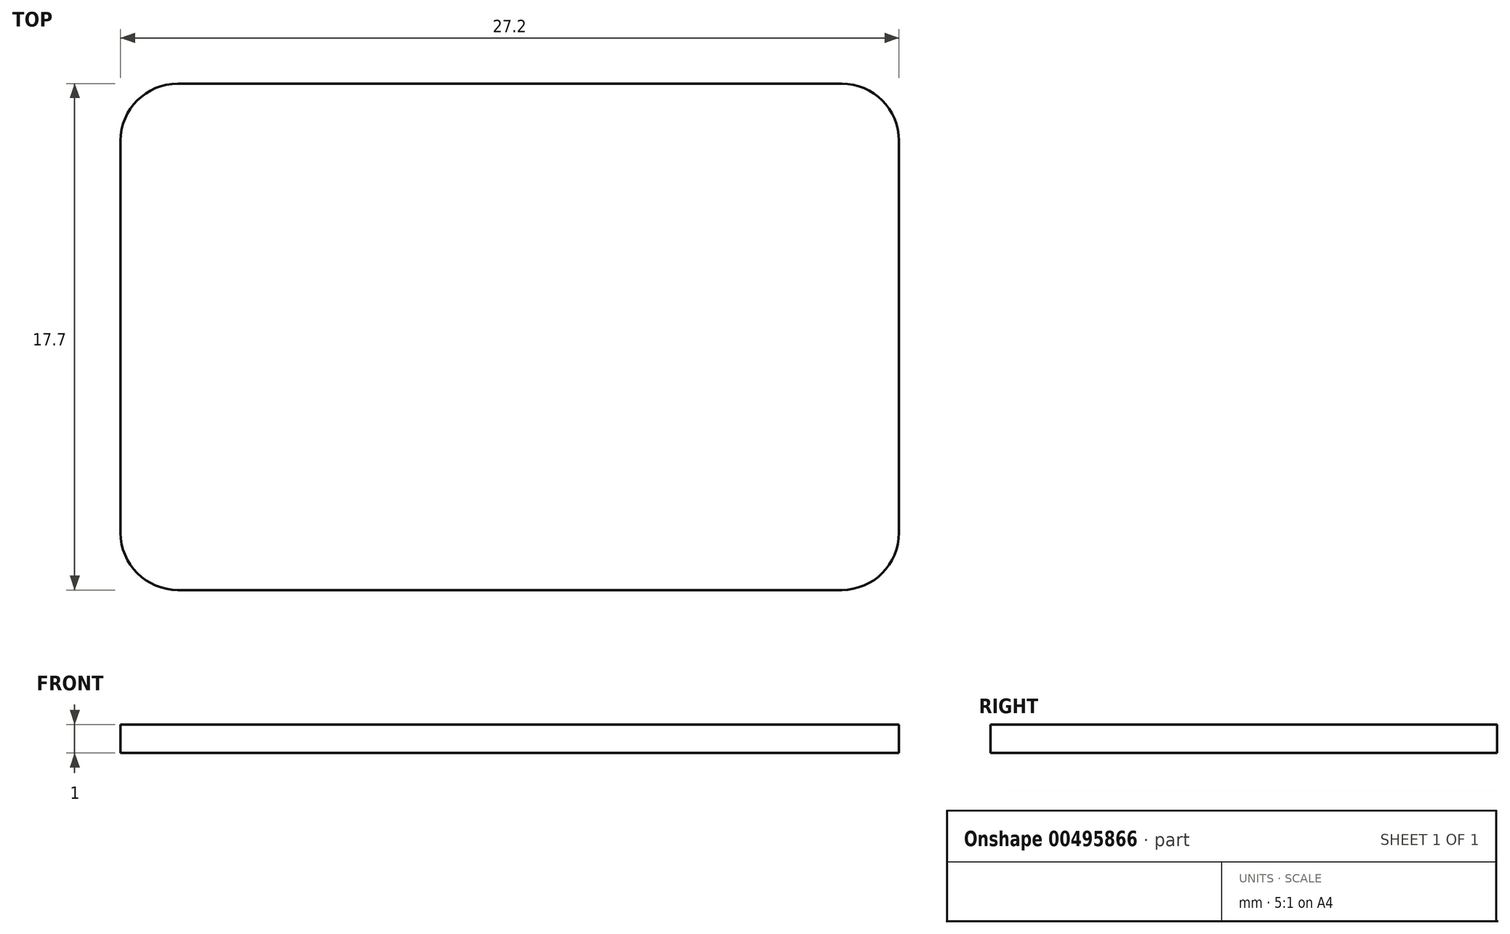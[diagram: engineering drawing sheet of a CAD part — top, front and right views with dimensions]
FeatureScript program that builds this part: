
annotation { "Feature Type Name" : "Feature", "Feature Type Description" : "" }
export const myFeature = defineFeature(function(context is Context, id is Id, definition is map)
    precondition{}
    {
        {
            var Q0;
            Q0=qCreatedBy(makeId("Top.planeOp"),FACE);
            var sketch = newSketch(context, id + "F0", { "sketchPlane" : qUnion([Q0])});
            skLineSegment(sketch, "E0.bottom", {"start": v(11.6, 8.85) * mm, "end": v(-11.6, 8.85) * mm});
            skLineSegment(sketch, "E0.top", {"start": v(11.6, -8.85) * mm, "end": v(-11.6, -8.85) * mm});
            skLineSegment(sketch, "E0.left", {"start": v(13.6, 6.85) * mm, "end": v(13.6, -6.85) * mm});
            skLineSegment(sketch, "E0.right", {"start": v(-13.6, 6.85) * mm, "end": v(-13.6, -6.85) * mm});
            skPoint(sketch, "E0.middle", {"position": v(0, 0) * mm});
            skPoint(sketch, "E1.visualSharp", {"position": v(13.6, 8.85) * mm});
            skArc(sketch, "E1.filletArc", {"start": v(13.6, 6.85) * mm, "mid": v(13.01, 8.26) * mm, "end": v(11.6, 8.85) * mm});
            skPoint(sketch, "E2.visualSharp", {"position": v(13.6, -8.85) * mm});
            skArc(sketch, "E2.filletArc", {"start": v(11.6, -8.85) * mm, "mid": v(13.01, -8.26) * mm, "end": v(13.6, -6.85) * mm});
            skPoint(sketch, "E3.visualSharp", {"position": v(-13.6, -8.85) * mm});
            skArc(sketch, "E3.filletArc", {"start": v(-13.6, -6.85) * mm, "mid": v(-13.01, -8.26) * mm, "end": v(-11.6, -8.85) * mm});
            skPoint(sketch, "E4.visualSharp", {"position": v(-13.6, 8.85) * mm});
            skArc(sketch, "E4.filletArc", {"start": v(-11.6, 8.85) * mm, "mid": v(-13.01, 8.26) * mm, "end": v(-13.6, 6.85) * mm});
            skSolve(sketch);
        }
        {
            var Q0;
            Q0=makeQuery(id+"F0.imprint","IMPRINT",FACE,{"disambiguationData":[TD([[makeQuery(id+"F0.imprint","IMPRINT",EDGE,{"derivedFrom":sQuery(id+"F0.wireOp",EDGE,"E0.bottom")}),1.0]])]});
            extrude(context, id + "F1", {"entities" : qUnion([Q0]), "depth" : 1 * mm, "offsetDistance" : 25 * mm});
        }
    });
